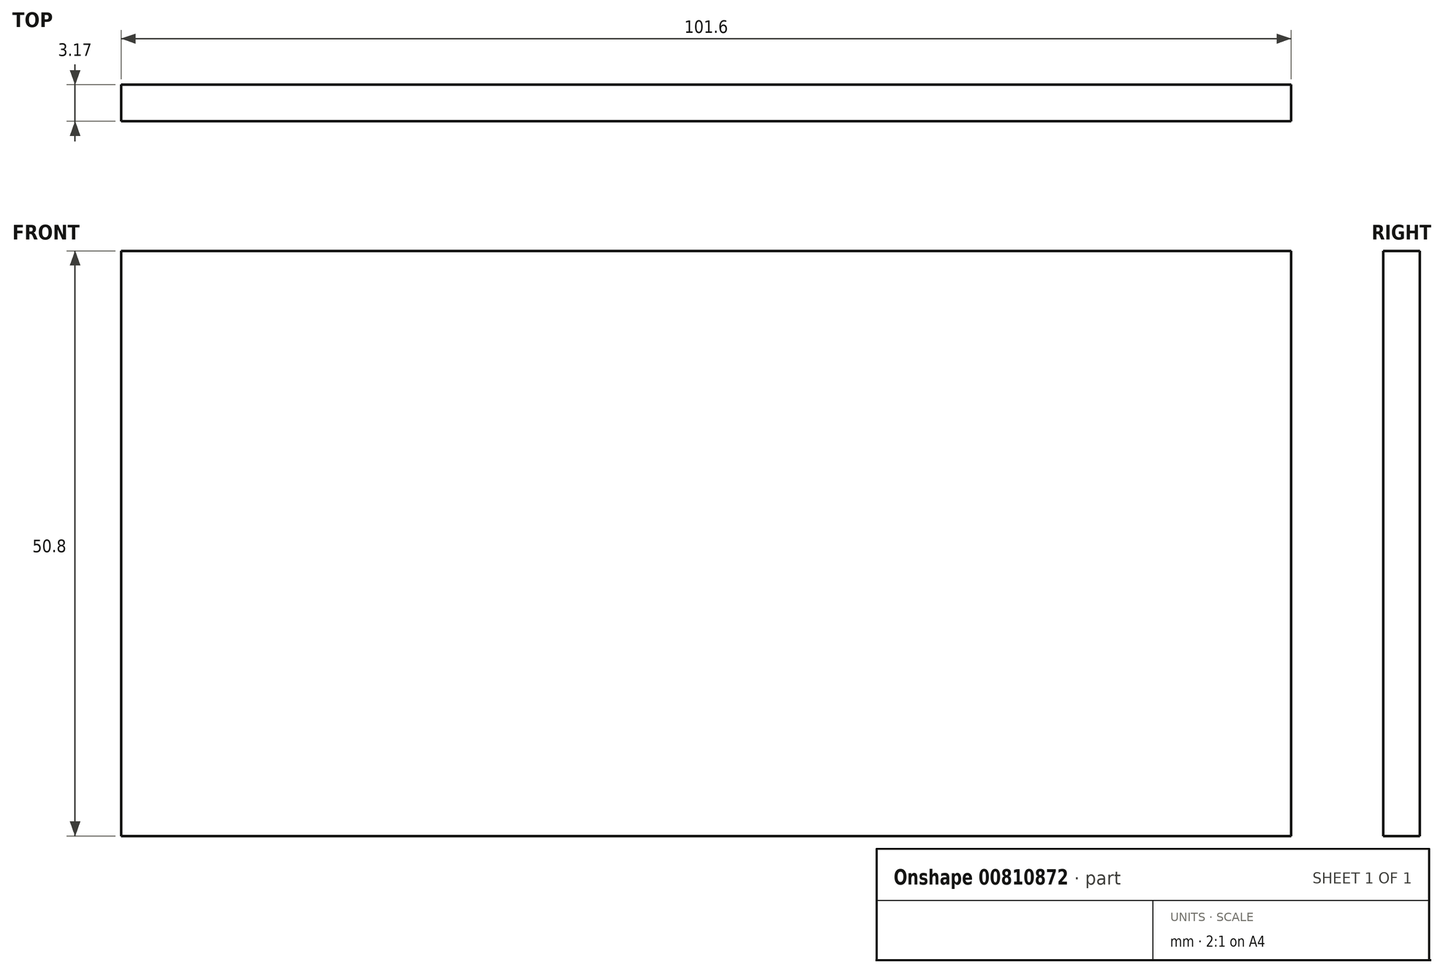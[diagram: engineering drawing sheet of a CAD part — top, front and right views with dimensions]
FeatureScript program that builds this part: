
annotation { "Feature Type Name" : "Feature", "Feature Type Description" : "" }
export const myFeature = defineFeature(function(context is Context, id is Id, definition is map)
    precondition{}
    {
        {
            var Q0;
            Q0=qCreatedBy(makeId("Front.planeOp"),FACE);
            var sketch = newSketch(context, id + "F0", { "sketchPlane" : qUnion([Q0])});
            skLineSegment(sketch, "E0.bottom", {"start": v(-78.22, 52.02) * mm, "end": v(23.38, 52.02) * mm});
            skLineSegment(sketch, "E0.top", {"start": v(-78.22, 1.22) * mm, "end": v(23.38, 1.22) * mm});
            skLineSegment(sketch, "E0.left", {"start": v(-78.22, 52.02) * mm, "end": v(-78.22, 1.22) * mm});
            skLineSegment(sketch, "E0.right", {"start": v(23.38, 52.02) * mm, "end": v(23.38, 1.22) * mm});
            skSolve(sketch);
        }
        {
            var Q0;
            Q0 = qSketchRegion(id + "F0", true);
            extrude(context, id + "F1", {"entities" : qUnion([Q0]), "depth" : 3.17 * mm, "offsetDistance" : 25.4 * mm});
        }
    });
